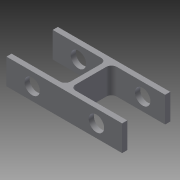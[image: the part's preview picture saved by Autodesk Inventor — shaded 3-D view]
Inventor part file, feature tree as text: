
AUTODESK INVENTOR PART (.ipt)
format: ipt  version: 2015 (Build 190159000, 159)  size: 120,320 bytes
history: native  units: mm
features: extrude x2, sketch x2, fillet x1
ambient origin geometry x8: Origin, YZ Plane, XZ Plane, XY Plane, X Axis, Y Axis, Z Axis, Center Point
bodies: Solid1 (feature_tree)
feature tree (5):
  extrude  "Extrusion1"  Depth=45.0mm
  extrude  "Extrusion2"  Depth=2.0mm
  fillet  "Fillet1"  Radius=1.0mm
  sketch  "Sketch1"  dims[d0=2.0mm d1=45.0mm]
  sketch  "Sketch2"  dims[d2=2.0mm d3=1.0mm d4=1.0mm d5=20.0mm d6=10.0mm d7=0.0mm d8=6.0mm d9=6.0mm d10=10.0mm d11=10.0mm d12=5.0mm d13=5.0mm d14=20.0mm d15=0.0mm d16=2.0mm]
